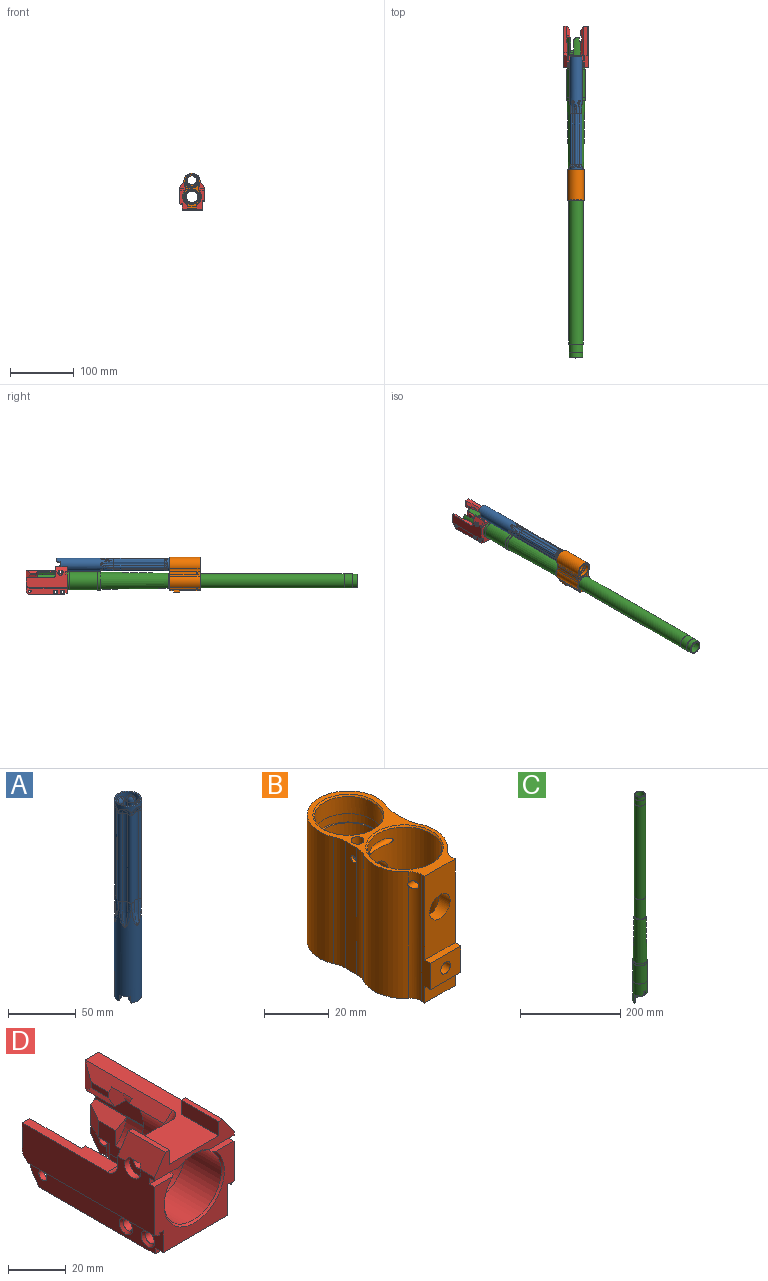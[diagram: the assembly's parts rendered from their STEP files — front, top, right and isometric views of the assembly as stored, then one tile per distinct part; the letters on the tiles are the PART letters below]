
ASSEMBLY  parts=4 mates=1
PART A: 93 faces, bbox 21.6x22x178.2 mm
  f0: plane 4.59x1.61mm, normal (0.87,0.5,0), area 5.5mm2, adj f4,f5,f6,f7
  f1: plane 4.59x1.61mm, normal (0.87,0.5,0), area 5.5mm2, adj f4,f7,f8,f9
  f2: plane 4.59x1.61mm, normal (-0.87,-0.5,0), area 5.5mm2, adj f4,f10,f11,f12
  f3: plane 4.59x1.61mm, normal (-0.87,-0.5,0), area 5.5mm2, adj f4,f12,f13,f14
  f4: cylinder r=10mm len=90.44mm, axis (0,0,1), area 4506.4mm2, adj f0,f1,f2,f3,f5,f7,f9,f10
  f5: plane 4.49x2.72mm, normal (0.43,-0.75,-0.5), area 4.1mm2, adj f0,f4,f6,f16,f76
  f6: plane 1.37x0.31mm, normal (0.5,-0.87,0), area 0.5mm2, adj f0,f5,f7,f76
  f7: plane 7.55x4.36mm, normal (0,0,-1), area 6.5mm2, adj f0,f1,f4,f6,f8,f76
  f8: plane 1.37x0.31mm, normal (-0.5,0.87,0), area 0.5mm2, adj f1,f7,f9,f76
  f9: plane 4.49x3.08mm, normal (-0.43,0.75,-0.5), area 4.1mm2, adj f1,f4,f8,f15,f76
  f10: plane 4.49x2.72mm, normal (-0.43,0.75,-0.5), area 4.1mm2, adj f2,f4,f11,f15,f76
  f11: plane 1.37x0.31mm, normal (-0.5,0.87,0), area 0.5mm2, adj f2,f10,f12,f76
  f12: plane 7.55x4.36mm, normal (0,0,-1), area 6.5mm2, adj f2,f3,f4,f11,f13,f76
  f13: plane 1.37x0.31mm, normal (0.5,-0.87,0), area 0.5mm2, adj f3,f12,f14,f76
  f14: plane 4.42x3.01mm, normal (0.43,-0.75,-0.5), area 4.1mm2, adj f3,f4,f13,f16,f76
  f15: plane 15x10mm, normal (0,0,-1), area 19.3mm2, adj f4,f9,f10,f76
  f16: plane 15x10mm, normal (0,0,-1), area 19.3mm2, adj f4,f5,f14,f76
  f17: plane 20x20mm, normal (0,0,1), area 59.7mm2, adj f77,f85
  f18: bspline ~7.79x5.5mm, area 20.9mm2, adj f22,f30,f77,f80
  f19: bspline ~21.79x7.79mm, area 62.6mm2, adj f21,f30,f76,f80
  f20: cylinder r=4.48mm len=79.56mm, axis (0,0,-1), area 483.2mm2, adj f21,f22,f30,f80
  f21: torus R=96.52mm, axis (0.5,-0.87,0), area 103.9mm2, adj f19,f20
  f22: torus R=1.52mm, axis (0.5,-0.87,0), area 22.4mm2, adj f18,f20
  f23: bspline ~8.66x5.5mm, area 32.8mm2, adj f27,f36,f85,f88
  f24: bspline ~21.79x8.66mm, area 103.9mm2, adj f4,f26,f36,f88
  f25: cylinder r=3.48mm len=79.56mm, axis (0,0,-1), area 375.4mm2, adj f26,f27,f36,f88
  f26: torus R=96.52mm, axis (0.5,-0.87,0), area 78.7mm2, adj f24,f25
  f27: torus R=1.52mm, axis (0.5,-0.87,0), area 14.5mm2, adj f23,f25
  f28: bspline ~7.79x5.5mm, area 20.9mm2, adj f30,f33,f42,f77
  f29: bspline ~21.79x7.79mm, area 62.6mm2, adj f30,f32,f42,f76
  f30: cylinder r=1.5mm len=79.56mm, axis (0,0,-1), area 286.6mm2, adj f18,f19,f20,f28,f29,f31
  f31: cylinder r=4.48mm len=79.56mm, axis (0,0,-1), area 483.2mm2, adj f30,f32,f33,f42
  f32: torus R=96.52mm, axis (-0.5,-0.87,0), area 103.9mm2, adj f29,f31
  f33: torus R=1.52mm, axis (-0.5,-0.87,0), area 22.4mm2, adj f28,f31
  f34: bspline ~8.66x5.5mm, area 32.8mm2, adj f36,f39,f48,f85
  f35: bspline ~21.79x8.66mm, area 103.9mm2, adj f4,f36,f38,f48
  f36: cylinder r=2.5mm len=79.56mm, axis (0,0,-1), area 477.7mm2, adj f23,f24,f25,f34,f35,f37
  f37: cylinder r=3.48mm len=79.56mm, axis (0,0,-1), area 375.4mm2, adj f36,f38,f39,f48
  f38: torus R=96.52mm, axis (-0.5,-0.87,0), area 78.7mm2, adj f35,f37
  f39: torus R=1.52mm, axis (-0.5,-0.87,0), area 14.5mm2, adj f34,f37
  f40: bspline ~9x5.5mm, area 20.9mm2, adj f42,f45,f54,f77
  f41: bspline ~21.79x9mm, area 62.6mm2, adj f42,f44,f54,f76
  f42: cylinder r=1.5mm len=79.56mm, axis (0,0,-1), area 286.6mm2, adj f28,f29,f31,f40,f41,f43
  f43: cylinder r=4.48mm len=79.56mm, axis (0,0,-1), area 483.2mm2, adj f42,f44,f45,f54
  f44: torus R=96.52mm, axis (-1,0,0), area 104mm2, adj f41,f43
  f45: torus R=1.52mm, axis (-1,0,0), area 22.4mm2, adj f40,f43
  f46: bspline ~10x5.5mm, area 32.8mm2, adj f48,f51,f60,f85
  f47: bspline ~21.79x10mm, area 103.9mm2, adj f4,f48,f50,f60
  f48: cylinder r=2.5mm len=79.56mm, axis (0,0,-1), area 477.7mm2, adj f34,f35,f37,f46,f47,f49
  f49: cylinder r=3.48mm len=79.56mm, axis (0,0,-1), area 375.4mm2, adj f48,f50,f51,f60
  f50: torus R=96.52mm, axis (-1,0,0), area 78.7mm2, adj f47,f49
  f51: torus R=1.52mm, axis (-1,0,0), area 14.5mm2, adj f46,f49
  f52: bspline ~7.79x5.5mm, area 20.9mm2, adj f54,f57,f66,f77
  f53: bspline ~21.79x7.79mm, area 62.6mm2, adj f54,f56,f66,f76
  f54: cylinder r=1.5mm len=79.56mm, axis (0,0,-1), area 286.6mm2, adj f40,f41,f43,f52,f53,f55
  f55: cylinder r=4.48mm len=79.56mm, axis (0,0,-1), area 483.2mm2, adj f54,f56,f57,f66
  f56: torus R=96.52mm, axis (-0.5,0.87,0), area 103.9mm2, adj f53,f55
  f57: torus R=1.52mm, axis (-0.5,0.87,0), area 22.4mm2, adj f52,f55
  f58: bspline ~8.66x5.5mm, area 32.8mm2, adj f60,f63,f72,f85
  f59: bspline ~21.79x8.66mm, area 103.9mm2, adj f4,f60,f62,f71,f72
  f60: cylinder r=2.5mm len=79.56mm, axis (0,0,-1), area 477.7mm2, adj f46,f47,f49,f58,f59,f61
  f61: cylinder r=3.48mm len=79.56mm, axis (0,0,-1), area 375.4mm2, adj f60,f62,f63,f72
  f62: torus R=96.52mm, axis (-0.5,0.87,0), area 78.7mm2, adj f59,f61
  f63: torus R=1.52mm, axis (-0.5,0.87,0), area 14.5mm2, adj f58,f61
  f64: bspline ~7.79x5.5mm, area 20.9mm2, adj f66,f69,f77,f81
  f65: bspline ~21.79x7.79mm, area 62.6mm2, adj f66,f68,f76,f81
  f66: cylinder r=1.5mm len=79.56mm, axis (0,0,-1), area 286.6mm2, adj f52,f53,f55,f64,f65,f67
  f67: cylinder r=4.48mm len=79.56mm, axis (0,0,-1), area 483.2mm2, adj f66,f68,f69,f81
  f68: torus R=96.52mm, axis (0.5,0.87,0), area 103.9mm2, adj f65,f67
  f69: torus R=1.52mm, axis (0.5,0.87,0), area 22.4mm2, adj f64,f67
  f70: bspline ~8.66x5.5mm, area 32.8mm2, adj f72,f75,f85,f89
  f71: bspline ~21.79x8.66mm, area 103.9mm2, adj f4,f59,f72,f74,f89
  f72: cylinder r=2.5mm len=79.56mm, axis (0,0,-1), area 477.7mm2, adj f58,f59,f61,f70,f71,f73
  f73: cylinder r=3.48mm len=79.56mm, axis (0,0,-1), area 375.4mm2, adj f72,f74,f75,f89
  f74: torus R=96.52mm, axis (0.5,0.87,0), area 78.7mm2, adj f71,f73
  f75: torus R=1.52mm, axis (0.5,0.87,0), area 14.5mm2, adj f70,f73
  f76: cylinder r=9mm len=90.44mm, axis (0,0,1), area 4077.3mm2, adj f5,f6,f7,f8,f9,f10,f11,f12
  f77: cylinder r=9mm len=18mm, axis (0,0,1), area 211.7mm2, adj f17,f18,f28,f40,f52,f64,f78
  f78: bspline ~9x5.5mm, area 20.9mm2, adj f77,f80,f81,f84
  f79: bspline ~21.79x9mm, area 62.6mm2, adj f76,f80,f81,f83
  f80: cylinder r=1.5mm len=79.56mm, axis (0,0,1), area 286.6mm2, adj f18,f19,f20,f78,f79,f82
  f81: cylinder r=1.5mm len=79.56mm, axis (0,0,-1), area 286.6mm2, adj f64,f65,f67,f78,f79,f82
  f82: cylinder r=4.48mm len=79.56mm, axis (0,0,-1), area 483.2mm2, adj f80,f81,f83,f84
  f83: torus R=96.52mm, axis (1,0,0), area 104mm2, adj f79,f82
  f84: torus R=1.52mm, axis (1,0,0), area 22.4mm2, adj f78,f82
  f85: cylinder r=10mm len=20mm, axis (0,0,1), area 235.3mm2, adj f17,f23,f34,f46,f58,f70,f86
  f86: bspline ~10x5.5mm, area 32.8mm2, adj f85,f88,f89,f92
  f87: bspline ~21.79x10mm, area 103.9mm2, adj f4,f88,f89,f91
  f88: cylinder r=2.5mm len=79.56mm, axis (0,0,1), area 477.7mm2, adj f23,f24,f25,f86,f87,f90
  f89: cylinder r=2.5mm len=79.56mm, axis (0,0,-1), area 477.7mm2, adj f70,f71,f73,f86,f87,f90
  f90: cylinder r=3.48mm len=79.56mm, axis (0,0,-1), area 375.4mm2, adj f88,f89,f91,f92
  f91: torus R=96.52mm, axis (1,0,0), area 78.7mm2, adj f87,f90
  f92: torus R=1.52mm, axis (1,0,0), area 14.5mm2, adj f86,f90
PART B: 43 faces, bbox 26.5x55.3x51 mm
  f0: cylinder r=10.5mm len=31mm, axis (0,0,-1), area 2006.3mm2, adj f1,f2,f3
  f1: plane 22x22mm, normal (0,0,1), area 33.8mm2, adj f0,f4
  f2: plane 22x22mm, normal (0,0,-1), area 33.8mm2, adj f0,f5
  f3: cylinder r=3.5mm len=7mm, axis (0,-1,0), area 69.6mm2, adj f0,f6
  f4: cylinder r=11mm len=22mm, axis (0,0,-1), area 241.9mm2, adj f1,f7
  f5: cylinder r=11mm len=22mm, axis (0,0,1), area -337.8mm2, adj f2,f8,f9
  f6: cylinder r=11.5mm len=47mm, axis (0,0,-1), area 3222.9mm2, adj f3,f10,f11,f12,f13,f14,f15
  f7: plane 22x22mm, normal (0,0,-1), area 33.8mm2, adj f4,f16
  f8: cylinder r=1.75mm len=4.34mm, axis (-0.87,0.5,0), area 22.5mm2, adj f5,f17,f18
  f9: plane 22x22mm, normal (0,0,1), area 215mm2, adj f5,f19
  f10: cone r=11.5mm half-angle=45deg, axis (0,0,1), area 52.2mm2, adj f6,f39
  f11: cone r=12mm half-angle=45deg, axis (0,0,-1), area 52.2mm2, adj f6,f40
  f12: cylinder r=4.5mm len=9mm, axis (0,-1,0), area 125.2mm2, adj f6,f20
  f13: cylinder r=1.5mm len=17.44mm, axis (1,0,0), area 100.2mm2, adj f6,f21,f22,f23,f24
  f14: cylinder r=1.25mm len=21.5mm, axis (1,0,0), area 119.8mm2, adj f6,f25,f26,f27,f28,f41
  f15: cylinder r=2.12mm len=6.67mm, axis (0,-1,0), area 87.8mm2, adj f6,f29
  f16: cylinder r=10.5mm len=21mm, axis (0,0,-1), area 428.8mm2, adj f7,f30
  f17: cylinder r=10mm len=48mm, axis (0,0,-1), area 193.6mm2, adj f8,f18,f39,f40,f41
  f18: cylinder r=12.75mm len=48mm, axis (0,0,-1), area 2439mm2, adj f8,f17,f39,f40,f42
  f19: cylinder r=7.25mm len=14.5mm, axis (0,0,-1), area 216.4mm2, adj f9,f31
  f20: plane 31.75x13.25mm, normal (0,-1,0), area 357.1mm2, adj f12,f32,f33,f34,f39
  f21: cylinder r=5mm len=48mm, axis (0,0,-1), area 203.1mm2, adj f13,f22,f33,f39,f40
  f22: cylinder r=13.25mm len=48mm, axis (0,0,-1), area 857.1mm2, adj f13,f21,f27,f39,f40
  f23: cylinder r=13.25mm len=48mm, axis (0,0,-1), area 857.1mm2, adj f13,f24,f26,f39,f40
  f24: cylinder r=5mm len=48mm, axis (0,0,-1), area 203.1mm2, adj f13,f23,f34,f39,f40
  f25: plane 48x4.78mm, normal (-1,0,0), area 224.8mm2, adj f14,f26,f39,f40,f42
  f26: cylinder r=10mm len=48mm, axis (0,0,-1), area 224.4mm2, adj f14,f23,f25,f39,f40
  f27: cylinder r=10mm len=48mm, axis (0,0,-1), area 224.4mm2, adj f14,f22,f39,f40,f41
  f28: cylinder r=2mm len=17mm, axis (0,0,1), area 200.4mm2, adj f14,f35,f39
  f29: plane 13.25x10mm, normal (0,-1,0), area 118.3mm2, adj f15,f32,f33,f34,f36
  f30: cone r=11mm half-angle=45deg, axis (0,0,1), area 47.8mm2, adj f16,f39
  f31: plane 18x18mm, normal (0,0,-1), area 89.3mm2, adj f19,f37
  f32: plane 13.25x2.5mm, normal (0,0,1), area 33.1mm2, adj f20,f29,f33,f34
  f33: plane 48x3.91mm, normal (1,0,0), area 92.5mm2, adj f20,f21,f29,f32,f36,f38,f39,f40
  f34: plane 48x3.91mm, normal (-1,0,0), area 92.5mm2, adj f20,f24,f29,f32,f36,f38,f39,f40
  f35: plane 4x4mm, normal (0,0,1), area 12.6mm2, adj f28
  f36: plane 13.25x2.5mm, normal (0,0,-1), area 33.1mm2, adj f29,f33,f34,f38
  f37: cylinder r=9mm len=18mm, axis (0,0,1), area 169.6mm2, adj f31,f40
  f38: plane 13.25x6.25mm, normal (0,-1,0), area 82.8mm2, adj f33,f34,f36,f40
  f39: plane 52.82x26.5mm, normal (0,0,1), area 300.7mm2, adj f10,f17,f18,f20,f21,f22,f23,f24
  f40: plane 52.82x26.5mm, normal (0,0,-1), area 438.9mm2, adj f11,f17,f18,f21,f22,f23,f24,f25
  f41: plane 48x4.78mm, normal (1,0,0), area 224.8mm2, adj f14,f17,f27,f39,f40
  f42: cylinder r=10mm len=48mm, axis (0,0,-1), area 202.8mm2, adj f18,f25,f39,f40
PART C: 52 faces, bbox 29.1x29.1x504.1 mm
  f0: cylinder r=14mm len=50mm, axis (0,0,-1), area 3052.6mm2, adj f4,f5,f6,f7,f26,f30,f31,f32
  f1: plane 22.06x13.31mm, normal (0,0,-1), area 1.6mm2, adj f2,f3,f40,f46
  f2: cylinder r=11.25mm len=22.83mm, axis (0,0,-1), area 349.5mm2, adj f1,f5,f7,f40,f41,f42,f43,f46
  f3: cone r=11.2mm half-angle=45.1deg, axis (0,0,-1), area 75.8mm2, adj f1,f27,f28,f39,f40,f44,f45,f46
  f4: plane 15.05x10.88mm, normal (0,0,-1), area 5mm2, adj f0,f5,f46,f51
  f5: plane 17.58x2.8mm, normal (0,-1,0), area 44.8mm2, adj f0,f2,f4,f42,f51
  f6: plane 8.41x5.38mm, normal (0,0,-1), area 22mm2, adj f0,f29,f31,f39
  f7: plane 6.1x3.18mm, normal (0,0,-1), area 11.9mm2, adj f0,f2,f41,f43
  f8: cylinder r=14.25mm len=44.5mm, axis (0,0,-1), area 3984.3mm2, adj f25,f26
  f9: cylinder r=14.5mm len=29mm, axis (0,0,1), area 432.8mm2, adj f23,f25
  f10: plane 23.5x23.5mm, normal (0,0,1), area 18.3mm2, adj f20,f22
  f11: plane 23x23mm, normal (0,0,1), area 24.9mm2, adj f19,f20
  f12: plane 22.3x22.3mm, normal (0,0,1), area 10.4mm2, adj f18,f19
  f13: plane 22x22mm, normal (0,0,1), area 42mm2, adj f15,f18
  f14: plane 19.88x19.88mm, normal (0,0,1), area 3.2mm2, adj f16,f17
  f15: cylinder r=10.38mm len=20.75mm, axis (0,0,1), area 554.1mm2, adj f13,f17
  f16: cone r=9.14mm half-angle=60deg, axis (0,0,1), area 51.8mm2, adj f14,f27
  f17: cone r=9.94mm half-angle=30deg, axis (0,0,-1), area 55.3mm2, adj f14,f15
  f18: cylinder r=11mm len=22mm, axis (0,0,1), area 881.2mm2, adj f12,f13
  f19: cylinder r=11.15mm len=228mm, axis (0,0,1), area 15973.1mm2, adj f11,f12
  f20: cylinder r=11.5mm len=47.5mm, axis (0,0,1), area 3397.4mm2, adj f10,f11,f35,f36,f37,f38
  f21: plane 23.99x23.99mm, normal (0,0,1), area 18.2mm2, adj f22,f24
  f22: cylinder r=11.75mm len=23.5mm, axis (0,0,1), area 92.3mm2, adj f10,f21
  f23: plane 29x29mm, normal (0,0,1), area 73mm2, adj f9,f24
  f24: cone r=13.67mm half-angle=0.9deg, axis (0,0,-1), area 8549mm2, adj f21,f23
  f25: plane 29x29mm, normal (0,0,-1), area 22.6mm2, adj f8,f9
  f26: plane 28.5x28.5mm, normal (0,0,-1), area 22.2mm2, adj f0,f8
  f27: cone r=10.3mm half-angle=0.1deg, axis (0,0,-1), area 29288.3mm2, adj f3,f16,f36,f37,f38
  f28: plane 18.12x8.13mm, normal (0,0,-1), area 1.1mm2, adj f3,f29,f39,f47
  f29: cylinder r=11.25mm len=22.83mm, axis (0,0,-1), area 151.7mm2, adj f6,f28,f31,f39,f47,f50
  f30: plane 15.05x10.88mm, normal (0,0,-1), area 5mm2, adj f0,f31,f47,f50
  f31: plane 22.73x2.8mm, normal (0,-1,0), area 59mm2, adj f0,f6,f29,f30,f50
  f32: cylinder r=2mm len=15.23mm, axis (1,0,0), area 77.5mm2, adj f0,f33,f34
  f33: plane 5.27x0.25mm, normal (0,0,-1), area 0.9mm2, adj f0,f32
  f34: plane 5.27x0.25mm, normal (0,0,1), area 0.9mm2, adj f0,f32
  f35: cylinder r=1.18mm len=10.13mm, axis (1,0,0), area 28.7mm2, adj f20
  f36: cylinder r=1mm len=4.56mm, axis (0,0.71,-0.71), area 15.4mm2, adj f20,f27
  f37: cylinder r=1mm len=4.57mm, axis (-0.12,0.7,-0.71), area 15.5mm2, adj f20,f27
  f38: cylinder r=1mm len=4.57mm, axis (0.12,0.7,-0.71), area 15.4mm2, adj f20,f27
  f39: plane 26.02x2.65mm, normal (0.87,0.5,0), area 70.9mm2, adj f0,f3,f6,f28,f29,f44
  f40: plane 23.52x2.65mm, normal (-0.87,-0.5,0), area 63.7mm2, adj f0,f1,f2,f3,f43,f44
  f41: plane 5.15x2.16mm, normal (0.71,-0.71,0), area 15.7mm2, adj f0,f2,f7,f42
  f42: plane 11.58x10.84mm, normal (0,0,-1), area 38.9mm2, adj f0,f2,f5,f41
  f43: plane 4.31x2.99mm, normal (-0.61,-0.35,-0.71), area 10.6mm2, adj f0,f2,f7,f40
  f44: plane 8.04x6.41mm, normal (-0.35,0.61,-0.71), area 33.8mm2, adj f0,f3,f39,f40
  f45: plane 3.14x0.47mm, normal (0,-1,0), area 0.5mm2, adj f3,f46,f49
  f46: plane 9.4x3.42mm, normal (-1,0,0), area 16.9mm2, adj f0,f1,f2,f3,f4,f45,f49,f51
  f47: plane 9.4x3.42mm, normal (1,0,0), area 16.9mm2, adj f0,f3,f28,f29,f30,f48,f49,f50
  f48: plane 3.13x0.47mm, normal (0,-1,0), area 0.5mm2, adj f3,f47,f49
  f49: plane 6.41x6.25mm, normal (0,-0.87,-0.5), area 44.8mm2, adj f0,f45,f46,f47,f48
  f50: cone r=11.25mm half-angle=45deg, axis (0,0,-1), area 63.2mm2, adj f29,f30,f31,f47
  f51: cone r=11.25mm half-angle=45deg, axis (0,0,-1), area 63.2mm2, adj f2,f4,f5,f46
PART D: 105 faces, bbox 39.1x65.1x44.6 mm
  f0: plane 62.32x1.6mm, normal (0,0,-1), area 99.7mm2, adj f38,f40,f65,f104
  f1: plane 13.65x2.25mm, normal (0,1,0), area 29.3mm2, adj f4,f9,f23,f39,f81,f100,f102
  f2: plane 27.5x11.47mm, normal (-1,0,0), area 194mm2, adj f3,f4,f6,f11,f12,f13,f77,f90
  f3: plane 9.57x5.27mm, normal (0,-1,0), area 24mm2, adj f2,f12,f102
  f4: plane 8.85x7mm, normal (-0.91,0.42,0), area 61.1mm2, adj f1,f2,f6,f102
  f5: plane 18.31x6.75mm, normal (0,-1,0), area 39.6mm2, adj f7,f91,f96,f99
  f6: plane 12.18x3.25mm, normal (0,0,-1), area 24.1mm2, adj f2,f4,f11,f81
  f7: plane 27.5x11.2mm, normal (1,0,0), area 169.9mm2, adj f5,f25,f75,f76,f77,f90,f91,f92
  f8: plane 21.25x6.5mm, normal (0,1,0), area 69.6mm2, adj f19,f21,f38,f58,f65,f74,f96,f97
  f9: plane 25.5x0.21mm, normal (0,0,1), area 5.3mm2, adj f1,f12,f13,f39,f93,f100
  f10: plane 4.84x0.03mm, normal (-1,0,0), area 0.2mm2, adj f67,f77,f90,f95
  f11: cylinder r=5mm len=9.5mm, axis (0,0,-1), area 37.7mm2, adj f2,f6,f22,f32,f77,f81,f82
  f12: cylinder r=16.5mm len=10mm, axis (0,-1,0), area 112.7mm2, adj f2,f3,f9,f13,f101
  f13: plane 26.1x8.9mm, normal (0,1,0), area 56.5mm2, adj f2,f9,f12,f14,f15,f18,f90,f93
  f14: plane 25.5x6mm, normal (0,0,-1), area 98.8mm2, adj f13,f16,f17,f18,f31,f93,f94
  f15: plane 42.75x4mm, normal (-0.71,0,0.71), area 197.7mm2, adj f13,f17,f18,f24,f30,f90,f94,f98
  f16: plane 13.75x5.2mm, normal (-0.87,0,-0.5), area 66.8mm2, adj f14,f17,f24,f94
  f17: plane 9.15x8.33mm, normal (0,-1,0), area 43.9mm2, adj f14,f15,f16,f18,f24
  f18: cylinder r=16.5mm len=10mm, axis (0,-1,0), area 116.3mm2, adj f13,f14,f15,f17
  f19: plane 41.75x5.89mm, normal (0,0,1), area 192mm2, adj f8,f21,f66,f90,f91,f92,f96
  f20: cylinder r=2mm len=34mm, axis (1,0,0), area 346.8mm2, adj f28,f85,f87
  f21: plane 65x24.75mm, normal (-1,0,0), area 1134.6mm2, adj f8,f19,f27,f33,f34,f40,f47,f65
  f22: plane 57x31.75mm, normal (0,0,-1), area 785.2mm2, adj f11,f23,f38,f39,f48,f58,f74,f75
  f23: plane 6x4mm, normal (0,0.83,-0.55), area 16.2mm2, adj f1,f22,f39,f81
  f24: plane 8.5x2.4mm, normal (-1,0,0), area 20.4mm2, adj f15,f16,f17,f94
  f25: cylinder r=4mm len=6.52mm, axis (0,0,-1), area 34.2mm2, adj f7,f67,f77,f90
  f26: plane 65x20.82mm, normal (1,0,0), area 1283.6mm2, adj f27,f31,f37,f40,f45,f59,f61,f62
  f27: plane 39x9.5mm, normal (0,-1,0), area 162.1mm2, adj f21,f26,f30,f33,f41,f42,f43,f44
  f28: cylinder r=14mm len=28mm, axis (0,-1,0), area 1465.8mm2, adj f20,f29,f47,f57,f68,f69,f70,f71
  f29: cone r=14mm half-angle=45deg, axis (0,-1,0), area 72.1mm2, adj f28,f40,f68,f72
  f30: plane 65.13x30.37mm, normal (0,0,1), area 753.3mm2, adj f15,f27,f31,f42,f43,f45,f46,f47
  f31: plane 17.82x8mm, normal (0,1,0), area 95.6mm2, adj f14,f26,f30,f59,f63,f64,f93,f94
  f32: cylinder r=2mm len=4mm, axis (1,0,0), area 28.3mm2, adj f11,f39,f81
  f33: plane 18.33x8.08mm, normal (-0.83,0,0.56), area 164.6mm2, adj f21,f27,f44,f47,f88,f89
  f34: plane 62.32x2.31mm, normal (-0.4,0,-0.92), area 154.2mm2, adj f21,f40,f65,f103
  f35: plane 62.32x1.6mm, normal (0,0,-1), area 99.7mm2, adj f36,f39,f40,f64
  f36: plane 62.32x1mm, normal (-1,0,0), area 61.3mm2, adj f35,f37,f40,f64
  f37: plane 62.32x1.4mm, normal (0.58,0,-0.81), area 105.4mm2, adj f26,f36,f40,f64
  f38: plane 65x16.75mm, normal (-1,0,0), area 666.8mm2, adj f0,f8,f22,f40,f48,f49,f52,f53
  f39: plane 65x19.65mm, normal (1,0,0), area 922.2mm2, adj f1,f9,f22,f23,f32,f35,f40,f48
  f40: plane 39x30mm, normal (0,-1,0), area 475.7mm2, adj f0,f21,f26,f29,f34,f35,f36,f37
  f41: plane 18.25x2mm, normal (0,0,1), area 36.5mm2, adj f27,f42,f45,f46
  f42: plane 18.25x6mm, normal (-1,0,0), area 109.5mm2, adj f27,f30,f41,f46
  f43: plane 18.25x6mm, normal (1,0,0), area 109.5mm2, adj f27,f30,f44,f47
  f44: plane 18.25x2mm, normal (0,0,1), area 36.5mm2, adj f27,f33,f43,f47
  f45: plane 21.08x8.08mm, normal (0.83,0,0.56), area 166.5mm2, adj f26,f27,f30,f41,f46,f60,f84,f86
  f46: plane 6.06x6mm, normal (0,1,0), area 24.2mm2, adj f30,f41,f42,f45
  f47: plane 36.75x34mm, normal (0,1,0), area 170.2mm2, adj f21,f28,f30,f33,f43,f44,f66,f90
  f48: plane 31.75x2.5mm, normal (0,-1,0), area 79.4mm2, adj f22,f38,f39,f49
  f49: plane 31.75x4mm, normal (0,0,-1), area 127mm2, adj f38,f39,f40,f48
  f50: cylinder r=2.25mm len=29.75mm, axis (1,0,0), area 420.6mm2, adj f52,f54
  f51: cylinder r=2.25mm len=29.75mm, axis (1,0,0), area 420.6mm2, adj f53,f55
  f52: cone r=3.25mm half-angle=45deg, axis (-1,0,0), area 24.4mm2, adj f38,f50
  f53: cone r=3.25mm half-angle=45deg, axis (-1,0,0), area 24.4mm2, adj f38,f51
  f54: cone r=2.25mm half-angle=45deg, axis (1,0,0), area 24.4mm2, adj f39,f50
  f55: cone r=2.25mm half-angle=45deg, axis (1,0,0), area 24.4mm2, adj f39,f51
  f56: cylinder r=2mm len=4mm, axis (1,0,0), area 28.3mm2, adj f38,f74,f75
  f57: cone r=14mm half-angle=45deg, axis (0,-1,0), area 14.5mm2, adj f27,f28,f69,f73
  f58: plane 6x4mm, normal (0,0.83,-0.55), area 16.2mm2, adj f8,f22,f38,f74
  f59: plane 5.12x2.24mm, normal (0,0.92,0.4), area 7.8mm2, adj f26,f31,f62,f63
  f60: cylinder r=2.75mm len=2.65mm, axis (1,0,0), area 3.3mm2, adj f30,f45,f61,f63
  f61: plane 35.35x1.4mm, normal (0,0,1), area 49.5mm2, adj f26,f60,f62,f63
  f62: cylinder r=7mm len=6.42mm, axis (1,0,0), area 11.4mm2, adj f26,f59,f61,f63
  f63: plane 46.65x11.32mm, normal (1,0,0), area 114.5mm2, adj f30,f31,f59,f60,f61,f62
  f64: cylinder r=6mm len=6mm, axis (1,0,0), area 19.4mm2, adj f26,f31,f35,f36,f37,f39,f93
  f65: cylinder r=6mm len=6mm, axis (-1,0,0), area 29.1mm2, adj f0,f8,f21,f34,f38,f103,f104
  f66: cylinder r=5mm len=9mm, axis (-1,0,0), area 53.6mm2, adj f19,f21,f47,f90
  f67: plane 13.25x4.84mm, normal (0,1,0), area 43.7mm2, adj f10,f25,f77,f90
  f68: plane 9.99x2.53mm, normal (0,0,1), area 24.5mm2, adj f21,f28,f29,f40,f70
  f69: plane 13.79x2.57mm, normal (0,0,-1), area 33.7mm2, adj f21,f27,f28,f57,f70
  f70: plane 13.72x2.5mm, normal (0,-1,0), area 29.1mm2, adj f21,f28,f68,f69
  f71: plane 13.72x2.5mm, normal (0,-1,0), area 29.1mm2, adj f26,f28,f72,f73
  f72: plane 9.99x2.53mm, normal (0,0,1), area 24.5mm2, adj f26,f28,f29,f40,f71
  f73: plane 13.78x2.57mm, normal (0,0,-1), area 33.7mm2, adj f26,f27,f28,f57,f71
  f74: plane 9.5x7.5mm, normal (1,0,0), area 47.6mm2, adj f8,f22,f56,f58,f75,f76
  f75: cylinder r=5mm len=9.5mm, axis (0,0,-1), area 37.7mm2, adj f7,f22,f56,f74,f76,f77,f78
  f76: plane 12.18x3.25mm, normal (0,0,-1), area 24.1mm2, adj f7,f74,f75,f97
  f77: plane 33.57x26.25mm, normal (0,0,-1), area 270.7mm2, adj f2,f7,f10,f11,f25,f67,f75,f78
  f78: plane 28.57x5mm, normal (1,0,0), area 142.9mm2, adj f22,f75,f77,f80
  f79: plane 16.25x5mm, normal (0,1,0), area 81.3mm2, adj f22,f77,f80,f83
  f80: cylinder r=5mm len=5mm, axis (0,0,-1), area 39.3mm2, adj f22,f77,f78,f79
  f81: plane 9.5x7.5mm, normal (-1,0,0), area 47.6mm2, adj f1,f6,f11,f22,f23,f32
  f82: plane 28.57x5mm, normal (-1,0,0), area 142.9mm2, adj f11,f22,f77,f83
  f83: cylinder r=5mm len=5mm, axis (0,0,-1), area 39.3mm2, adj f22,f77,f79,f82
  f84: plane 5.36x1.51mm, normal (0,0,-1), area 8.1mm2, adj f45,f85,f86
  f85: plane 8x6.97mm, normal (1,0,0), area 33.9mm2, adj f20,f84,f86
  f86: cylinder r=4mm len=8mm, axis (1,0,0), area 46.4mm2, adj f26,f45,f84,f85
  f87: plane 8x6.97mm, normal (-1,0,0), area 33.9mm2, adj f20,f88,f89
  f88: plane 5.36x1.51mm, normal (0,0,-1), area 8.1mm2, adj f33,f87,f89
  f89: cylinder r=4mm len=8mm, axis (-1,0,0), area 46.4mm2, adj f21,f33,f87,f88
  f90: cylinder r=14.5mm len=29mm, axis (0,-1,0), area 1106.8mm2, adj f2,f7,f10,f13,f15,f19,f25,f47
  f91: cylinder r=16.5mm len=18.31mm, axis (0,-1,0), area 205.7mm2, adj f5,f7,f19,f92
  f92: plane 18.31x6.75mm, normal (0,1,0), area 37.8mm2, adj f7,f19,f90,f91
  f93: plane 25.5x7.25mm, normal (-1,0,0), area 184.8mm2, adj f9,f13,f14,f31,f64
  f94: plane 11.6x7mm, normal (-0.87,0.5,0), area 61.7mm2, adj f14,f15,f16,f24,f31
  f95: cylinder r=4mm len=7.8mm, axis (0,0,-1), area 38.2mm2, adj f2,f10,f77,f90
  f96: plane 15.5x7.6mm, normal (1,0,0), area 117.8mm2, adj f5,f8,f19,f99
  f97: plane 8.58x7mm, normal (0.91,0.42,0), area 59mm2, adj f7,f8,f76,f99
  f98: bspline ~7.9x4mm, area 26.3mm2, adj f15,f30,f47,f90
  f99: plane 15.5x5.97mm, normal (0.5,0,0.87), area 93.8mm2, adj f5,f7,f8,f96,f97
  f100: plane 15.5x0.09mm, normal (-0.87,0,-0.5), area 1.6mm2, adj f1,f9,f101,f102
  f101: plane 0.13x0.07mm, normal (0,1,0), area 0mm2, adj f12,f100,f102
  f102: plane 15.5x5.35mm, normal (-0.5,0,0.87), area 82.5mm2, adj f1,f2,f3,f4,f100,f101
  f103: plane 59x0.34mm, normal (0,0,-1), area 20.1mm2, adj f34,f40,f65,f104
  f104: plane 62.32x1mm, normal (1,0,0), area 61.3mm2, adj f0,f40,f65,f103
PLACE A rot(axis=(0.93,0.26,-0.26),94.3deg) t=(1.59,19.69,51.8)mm
PLACE B rot(axis=(1,0,0),90deg) t=(1.59,-182.31,50.55)mm fixed
PLACE C rot(axis=(1,0,0),90deg) t=(1.59,-454.98,25.95)mm fixed
PLACE D t=(1.59,2.64,3.7)mm fixed
MATE cylindrical A.f4 <-> B.f19  axis (0,-1,0) through (1.59,-158.31,51.8)mm
